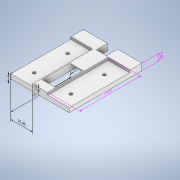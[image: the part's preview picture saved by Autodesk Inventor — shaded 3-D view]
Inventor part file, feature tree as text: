
AUTODESK INVENTOR PART (.ipt)
format: ipt  version: 2020 (Build 240168000, 168)  size: 241,664 bytes
history: native  units: mm
features: other x8, sketch x8, extrude x5, hole x2
ambient origin geometry x8: Origin, YZ Plane, XZ Plane, XY Plane, X Axis, Y Axis, Z Axis, Center Point
bodies: Solid1 (feature_tree)
feature tree (23):
  other  "Annotations"
  sketch  "Sketch1"  dims[d0=70.0mm d1=73.0mm]
  sketch  "Sketch2"  dims[d2=14.0mm d3=29.0mm]
  extrude  "Extrusion1"  Depth=70.0mm
  extrude  "Extrusion2"  Depth=29.0mm
  hole  "Hole1"  [1 undecoded]
  extrude  "Extrusion3"  Depth=3.0mm
  extrude  "Extrusion4"  Depth=2.61mm TaperAngle=0.0deg
  hole  "Hole2"  [1 undecoded]
  extrude  "Extrusion5"  Depth=15.0mm
  sketch  "Sketch3"  dims[d4=7.0mm d5=87.0mm]
  sketch  "Sketch4"  dims[d6=8.0mm d7=0.0mm d8=3.0mm]
  sketch  "Sketch5"  dims[d9=3.0mm d10=2.61mm d11=0.0mm]
  sketch  "Sketch10"  dims[d31=5.475mm d32=5.475mm]
  sketch  "Sketch12"  dims[d33=15.0mm d38=7.5mm]
  sketch  "Sketch13"  dims[d39=13.2mm d40=3.5mm d43=7.5mm d44=13.2mm d45=3.5mm d46=3.5mm d47=36.5mm d48=3.5mm d49=40.0mm d50=3.5mm d51=8.60806mm d52=10.0mm d53=2.0mm d54=14.3117mm d55=15.664mm d56=0.0mm d57=14.525mm d61=7.0mm d62=0.5mm d63=0.0mm d64=12.049942mm d72=7.0mm d73=10.0mm d74=1.4mm d75=1.4mm d76=7.0mm d77=0.0mm d78=12.049942mm d79=3.0mm d80=3.0mm d82=3.0mm d83=3.0mm d84=2.5mm d85=3.0mm d86=6.0mm d87=4.0mm d88=2.0mm d89=90.0deg d90=10.5mm d91=20.594885mm d93=10.0mm d94=0.0mm d15=6.837877mm d16=4.039262mm d17=5.39mm d18=0.0mm d19=10.0mm d20=2.61mm d24=0.0mm d25=10.0mm d26=15.0mm d28=0.0mm d29=10.0mm d30=25.950058mm d35=0.0mm d36=10.0mm d37=72.0mm d58=4.624248mm d59=6.476976mm d60=73.0mm d65=0.0mm d66=10.0mm d67=8.0mm]
  other  "Linear Dimension 1"
  other  "Linear Dimension 2"
  other  "Linear Dimension 4"
  other  "Linear Dimension 5"
  other  "Linear Dimension 6"
  other  "Linear Dimension 7"
  other  "Linear Dimension 8"
note: 2 required parameter values undecoded (feature->parameter linkage not recoverable at this tier; creation-order binding heuristic only, values carry confidence <= 0.55)
